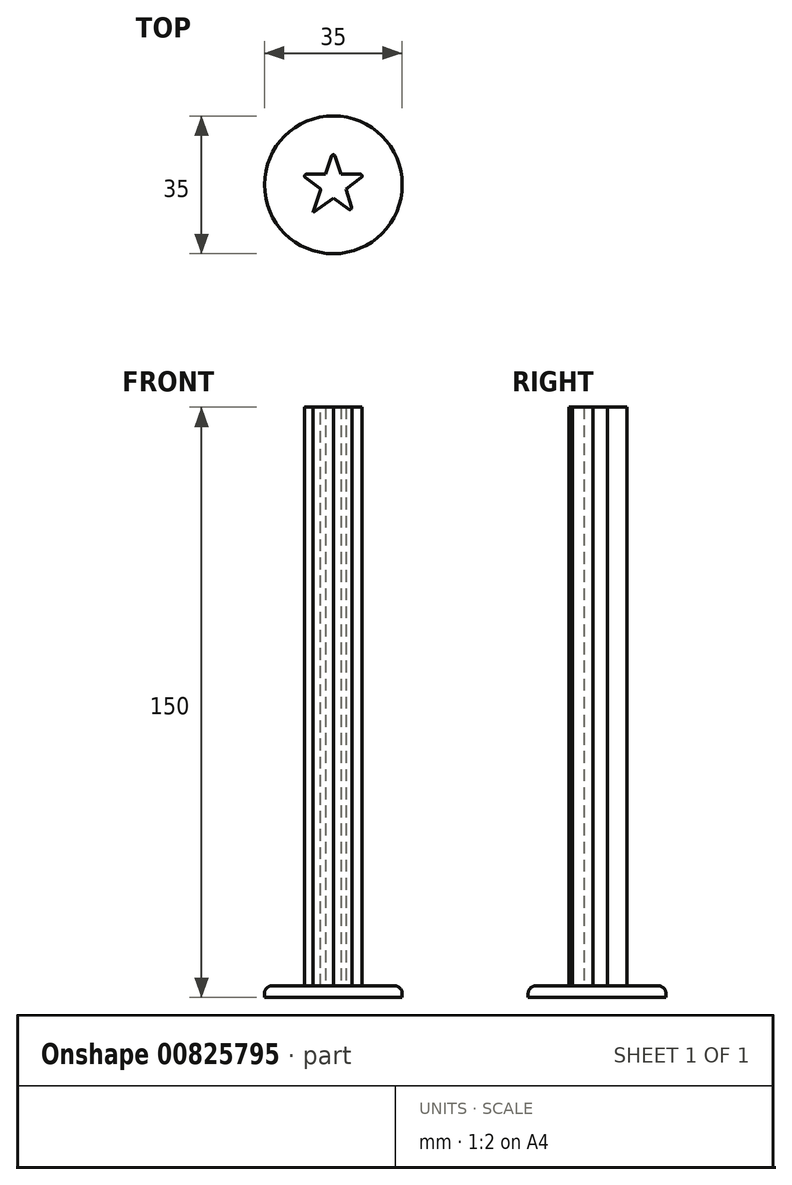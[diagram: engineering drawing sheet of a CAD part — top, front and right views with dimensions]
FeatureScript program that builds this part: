
annotation { "Feature Type Name" : "Feature", "Feature Type Description" : "" }
export const myFeature = defineFeature(function(context is Context, id is Id, definition is map)
    precondition{}
    {
        {
            var Q0;
            Q0=qCreatedBy(makeId("Top.planeOp"),FACE);
            var sketch = newSketch(context, id + "F0", { "sketchPlane" : qUnion([Q0])});
            skCircle(sketch, "E0.cCircle", {"center": v(0, 0) * mm, "radius": 8.75 * mm, "construction": true});
            skLineSegment(sketch, "E0.0", {"start": v(8.32, 2.7) * mm, "end": v(5.14, -7.08) * mm});
            skLineSegment(sketch, "E0.1", {"start": v(5.14, -7.08) * mm, "end": v(-5.14, -7.08) * mm});
            skLineSegment(sketch, "E0.2", {"start": v(-5.14, -7.08) * mm, "end": v(-8.32, 2.7) * mm});
            skLineSegment(sketch, "E0.3", {"start": v(-8.32, 2.7) * mm, "end": v(0, 8.75) * mm});
            skLineSegment(sketch, "E0.4", {"start": v(0, 8.75) * mm, "end": v(8.32, 2.7) * mm});
            skLineSegment(sketch, "E1", {"start": v(0, 8.75) * mm, "end": v(1.96, 2.7) * mm});
            skLineSegment(sketch, "E2", {"start": v(8.32, 2.7) * mm, "end": v(3.18, -1.03) * mm});
            skLineSegment(sketch, "E3", {"start": v(5.14, -7.08) * mm, "end": v(0, -3.34) * mm});
            skLineSegment(sketch, "E4", {"start": v(-8.32, 2.7) * mm, "end": v(-1.96, 2.7) * mm});
            skLineSegment(sketch, "E5", {"start": v(-5.14, -7.08) * mm, "end": v(-3.18, -1.03) * mm});
            skLineSegment(sketch, "E6.trimOffspring", {"start": v(1.96, 2.7) * mm, "end": v(8.32, 2.7) * mm});
            skLineSegment(sketch, "E7.trimOffspring", {"start": v(3.18, -1.03) * mm, "end": v(5.14, -7.08) * mm});
            skLineSegment(sketch, "E8.trimOffspring", {"start": v(0, -3.34) * mm, "end": v(-5.14, -7.08) * mm});
            skLineSegment(sketch, "E9.trimOffspring", {"start": v(-3.18, -1.03) * mm, "end": v(-8.32, 2.7) * mm});
            skLineSegment(sketch, "E10.trimOffspring", {"start": v(-1.96, 2.7) * mm, "end": v(0, 8.75) * mm});
            skSolve(sketch);
        }
        {
            var Q0;
            Q0=makeQuery(id+"F0.imprint","IMPRINT",FACE,{"disambiguationData":[TD([[makeQuery(id+"F0.imprint","IMPRINT",EDGE,{"derivedFrom":sQuery(id+"F0.wireOp",EDGE,"E1")}),-1.0]])]});
            extrude(context, id + "F1", {"entities" : qUnion([Q0]), "depth" : 150 * mm, "offsetDistance" : 25 * mm});
        }
        {
            var Q0;
            Q0=makeQuery(id+"F1.opExtrude","SWEPT_EDGE",EDGE,{"disambiguationData":[OSD([sQuery(id+"F0.wireOp",EDGE,"E0.2"),sQuery(id+"F0.wireOp",EDGE,"E0.3"),sQuery(id+"F0.wireOp",EDGE,"E4"),sQuery(id+"F0.wireOp",EDGE,"E9.trimOffspring")])]});
            var Q1;
            Q1=makeQuery(id+"F1.opExtrude","SWEPT_EDGE",EDGE,{"disambiguationData":[OSD([sQuery(id+"F0.wireOp",EDGE,"E5"),sQuery(id+"F0.wireOp",EDGE,"E9.trimOffspring")])]});
            var Q2;
            Q2=makeQuery(id+"F1.opExtrude","SWEPT_EDGE",EDGE,{"disambiguationData":[OSD([sQuery(id+"F0.wireOp",EDGE,"E0.0"),sQuery(id+"F0.wireOp",EDGE,"E0.1"),sQuery(id+"F0.wireOp",EDGE,"E3"),sQuery(id+"F0.wireOp",EDGE,"E7.trimOffspring")])]});
            var Q3;
            Q3=makeQuery(id+"F1.opExtrude","SWEPT_EDGE",EDGE,{"disambiguationData":[OSD([sQuery(id+"F0.wireOp",EDGE,"E0.3"),sQuery(id+"F0.wireOp",EDGE,"E0.4"),sQuery(id+"F0.wireOp",EDGE,"E1"),sQuery(id+"F0.wireOp",EDGE,"E10.trimOffspring")])]});
            var Q4;
            Q4=makeQuery(id+"F1.opExtrude","SWEPT_EDGE",EDGE,{"disambiguationData":[OSD([sQuery(id+"F0.wireOp",EDGE,"E0.0"),sQuery(id+"F0.wireOp",EDGE,"E0.4"),sQuery(id+"F0.wireOp",EDGE,"E2"),sQuery(id+"F0.wireOp",EDGE,"E6.trimOffspring")])]});
            fillet(context, id + "F2", {"entities" : qUnion([Q0, Q1, Q2, Q3, Q4]), "radius" : 0.5 * mm, "tangentPropagation" : true, "allowEdgeOverflow" : false});
        }
        {
            var Q0;
            Q0=qCreatedBy(makeId("Top.planeOp"),FACE);
            var sketch = newSketch(context, id + "F3", { "sketchPlane" : qUnion([Q0])});
            skCircle(sketch, "E11", {"center": v(0, 0) * mm, "radius": 17.5 * mm});
            skSolve(sketch);
        }
        {
            var Q0;
            Q0=makeQuery(id+"F3.imprint","IMPRINT",FACE,{"disambiguationData":[TD([[makeQuery(id+"F3.imprint","IMPRINT",EDGE,{"derivedFrom":sQuery(id+"F3.wireOp",EDGE,"E11")}),1.0]])]});
            extrude(context, id + "F4", {"entities" : qUnion([Q0]), "operationType" : NewBodyOperationType.ADD, "depth" : 3 * mm, "offsetDistance" : 25 * mm});
        }
        {
            var Q0;
            Q0=makeQuery(id+"F4.opExtrude","CAP_EDGE",EDGE,{"disambiguationData":[OSD([sQuery(id+"F3.wireOp",EDGE,"E11")])],"isStart":false});
            fillet(context, id + "F5", {"entities" : qUnion([Q0]), "radius" : 2 * mm, "tangentPropagation" : true, "allowEdgeOverflow" : false});
        }
    });
